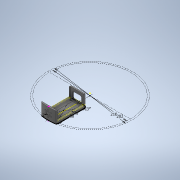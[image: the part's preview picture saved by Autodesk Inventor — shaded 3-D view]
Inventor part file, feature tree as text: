
AUTODESK INVENTOR PART (.ipt)
format: ipt  version: 2020 (Build 240168000, 168)  size: 408,576 bytes
history: native  units: mm
features: projected_geometry x27, sketch x9, extrude x9, other x5, fillet x1
ambient origin geometry x8: Origin, YZ Plane, XZ Plane, XY Plane, X Axis, Y Axis, Z Axis, Center Point
bodies: Body1 (feature_tree)
feature tree (51):
  other  "Твердое тело1"
  sketch  "Эскиз1"
  extrude  "Выдавливание3"  Depth=202.0mm
  other  "РабПлоскость1"
  extrude  "Выдавливание1"  Depth=35.0mm
  other  "РабПлоскость2"
  sketch  "Эскиз2"
  extrude  "Выдавливание4"  Depth=68.0mm
  extrude  "Выдавливание5"  Depth=2.0mm
  sketch  "Эскиз4"
  extrude  "Выдавливание6"  Depth=2.0mm
  extrude  "Выдавливание7"  Depth=3.0mm
  other  "РабПлоскость3"
  extrude  "Выдавливание8"  Depth=3.0mm
  other  "РабПлоскость4"
  extrude  "Выдавливание9"  Depth=210.0mm
  extrude  "Выдавливание10"  Depth=20.0mm TaperAngle=0.0deg
  sketch  "Эскиз9"
  fillet  "Сопряжение1"  Radius=1.5mm
  projected_geometry  "Спроецированная петля1"
  projected_geometry  "Спроецированная петля7"
  projected_geometry  "Спроецированная петля8"
  sketch  "Эскиз3"
  projected_geometry  "Спроецированная петля9"
  projected_geometry  "Спроецированная петля10"
  projected_geometry  "Спроецированная петля11"
  projected_geometry  "Спроецированная петля12"
  sketch  "Эскиз5"
  projected_geometry  "Спроецированная петля13"
  projected_geometry  "Спроецированная петля14"
  projected_geometry  "Спроецированная петля15"
  projected_geometry  "Спроецированная петля16"
  projected_geometry  "Спроецированная петля17"
  sketch  "Эскиз6"
  sketch  "Эскиз7"
  projected_geometry  "Спроецированная петля18"
  projected_geometry  "Спроецированная петля19"
  projected_geometry  "Спроецированная петля20"
  projected_geometry  "Спроецированная петля21"
  projected_geometry  "Спроецированная петля22"
  projected_geometry  "Спроецированная петля23"
  projected_geometry  "Спроецированная петля24"
  sketch  "Эскиз8"
  projected_geometry  "Спроецированная петля25"
  projected_geometry  "Спроецированная петля26"
  projected_geometry  "Спроецированная петля27"
  projected_geometry  "Спроецированная петля28"
  projected_geometry  "Спроецированная петля29"
  projected_geometry  "Спроецированная петля30"
  projected_geometry  "Спроецированная петля31"
  projected_geometry  "Спроецированная петля32"
